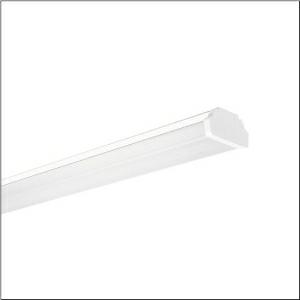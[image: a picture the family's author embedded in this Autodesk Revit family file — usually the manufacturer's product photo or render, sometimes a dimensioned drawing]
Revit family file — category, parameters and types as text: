
# Revit family: dus_r__31_gen_2_53bd812dv6dxd2_e925
name_source: partatom
category: Lighting Fixtures
units: mm (PartAtom-declared; Revit-internal decimal feet)

## family parameters
Cut with Voids When Loaded = No
Host = Face
Light Source = No
Part Type = Normal
Room Calculation Point = No
Round Connector Dimension = Use Diameter
Shared = No

## types (1)
- --- (1 x LED, 13280 lm, 74.9 W, 6500K)
    Apparent Load = 75 VA
    CIE Flux Codes = 47 80 95 93 100
    Color Rendering = 80
    Color Temperature = 6500K
    Default Elevation = 1800 mm
    Description = DUS® 31 Gen.2, luminaire insert, of sheet steel, coil coated, white, length: 1.535mm, width: 81mm, height: 90mm, 5x system unit, system units: 307mm, LED rated luminous flux: 13.280lm, light colour: 865, control gear: DALI 2, control gear: ECG DALI, with plug, 5-pole, with phase selection, mains connection: 220..240V, AC, 50/60Hz, rated input power: 75W, through-wiring accessed according to module size, primary optical cover: cover, of PMMA, light emission: direct distribution, primary light characteristic: symmetric, protection rating (complete): IP20, protection rating (LED compartment): IP50, insulation class (complete): insulation class I (protective earthing), certification: CE, ENEC, VDE, UKCA, impact resistance: IK03, permissible ambient temperature for indoor applications: -25..+35°C, corresponds to IFS (International Featured Standards) requirements for safety and quality in the food industry, reducing of maximum allowable ambient temperature of 5°C with ceiling mounting, packaging unit: 1 piece
    Height = 95 mm
    Lamp = 1 x LED
    Lamp Light Flux = 13280 lm
    Lamp Power = 74.9 W
    Lamp count = 1
    Length = 1535 mm
    Luminous efficacy = 177 lm/W
    Manufacturer = Siteco
    ModVariant = No
    Model = 53BD812DV6DXD2
    Mounting Place = Ceiling
    Mounting Type = Pendant
    Number of Poles = 1
    OnlyDefault = Yes
    Power Factor = 1
    Product Name = DUS® 31 Gen.2
    Product group = luminaire insert
    ProductGroupID = 902
    Protection Class = Protection class I
    Protection Degree = IP 20
    RLX_Detail_Level = 1
    RLX_Emergency_Light_Flux = 0 lm
    RLX_Emergency_Type = 0
    RLX_Emergency_Type_DB = No
    RlxData = <blob elided: 32217 chars, md5=f872acd5>
    Socket = socket
    Standby Power = 0 W
    System Light Flux = 13280 lm
    System Power = 75 W
    Type Comments = factory setting: luminous flux: 100 % | dim-lin: 254 | 511 mA
    Type Image = l_1319596.jpg
    URL = http://relux.com
    VarID = @adj_042312
    Voltage = 0 V
    Weight = 0.00 kg
    Width = 81 mm

## geometry (parser evidence)
native form markers: Blend x4, Sweep x15
no freeform markers — native parametric forms only
